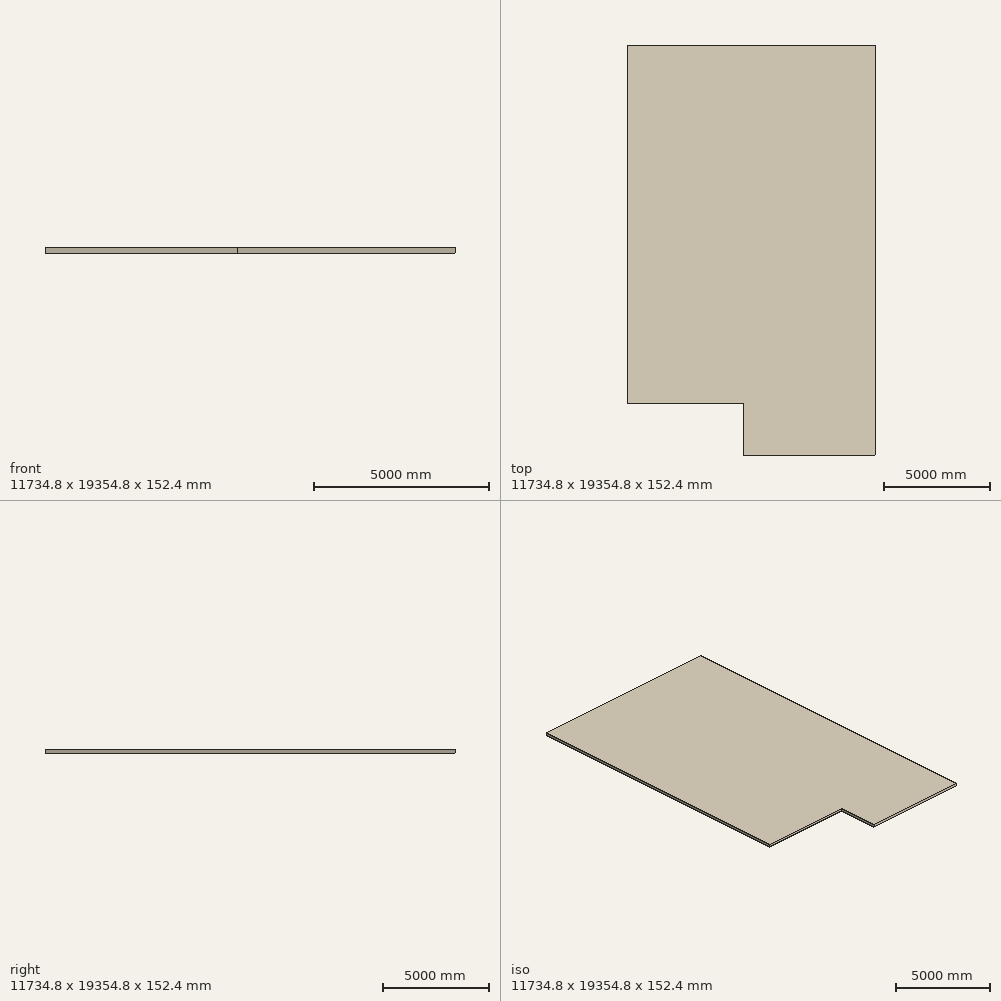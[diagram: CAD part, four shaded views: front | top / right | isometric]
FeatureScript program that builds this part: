
annotation { "Feature Type Name" : "Feature", "Feature Type Description" : "" }
export const myFeature = defineFeature(function(context is Context, id is Id, definition is map)
    precondition{}
    {
        {
            var Q0;
            Q0=qCreatedBy(makeId("Top.planeOp"),FACE);
            var sketch = newSketch(context, id + "F0", { "sketchPlane" : qUnion([Q0])});
            skLineSegment(sketch, "E0.bottom", {"start": v(-381, -8458.2) * mm, "end": v(-5867.4, -8458.2) * mm});
            skLineSegment(sketch, "E0.top", {"start": v(5867.4, 8458.2) * mm, "end": v(-5867.4, 8458.2) * mm});
            skLineSegment(sketch, "E0.left", {"start": v(5867.4, -10896.6) * mm, "end": v(5867.4, 8458.2) * mm});
            skLineSegment(sketch, "E0.right", {"start": v(-5867.4, -8458.2) * mm, "end": v(-5867.4, 8458.2) * mm});
            skPoint(sketch, "E0.middle", {"position": v(0, 0) * mm});
            skLineSegment(sketch, "E1", {"start": v(-381, -8458.2) * mm, "end": v(-381, -10896.6) * mm});
            skLineSegment(sketch, "E2", {"start": v(-381, -10896.6) * mm, "end": v(5867.4, -10896.6) * mm});
            skPoint(sketch, "E3.orphan", {"position": v(5867.4, -8458.2) * mm});
            skSolve(sketch);
        }
        {
            var Q0;
            Q0=makeQuery(id+"F0.imprint","IMPRINT",FACE,{"disambiguationData":[TD([[makeQuery(id+"F0.imprint","IMPRINT",EDGE,{"derivedFrom":sQuery(id+"F0.wireOp",EDGE,"E0.bottom")}),-1.0]])]});
            extrude(context, id + "F1", {"entities" : qUnion([Q0]), "depth" : 152.4 * mm});
        }
    });
